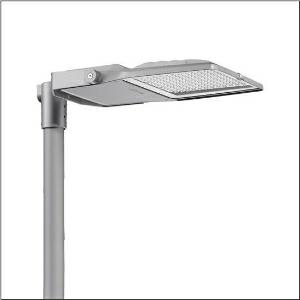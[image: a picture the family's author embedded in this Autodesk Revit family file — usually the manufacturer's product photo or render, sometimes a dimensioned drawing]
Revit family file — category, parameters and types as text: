
# Revit family: floodlight_fl_21_midi___pl33t_5xa7782f4f3a_2082
name_source: partatom
category: Lighting Fixtures
units: mm (PartAtom-declared; Revit-internal decimal feet)

## family parameters
Cut with Voids When Loaded = No
Host = Face
Light Source = No
Part Type = Normal
Room Calculation Point = No
Round Connector Dimension = Use Diameter
Shared = No

## types (1)
- --- (1 x LED, 36900 lm, 270.2 W, 4000K)
    Apparent Load = 270 VA
    CIE Flux Codes = 26 75 99 100 100
    Color Rendering = 70
    Color Temperature = 4000K
    Default Elevation = 1800 mm
    Description = Floodlight FL 21 midi, floodlight, primary light control with lens, of PMMA, primary optical cover: protective disc, of toughened safety glass, transparent, light distribution: PL33T, light emission: direct distribution, installation type: surface-mounted, LED, High Power LED, rated luminous flux: 36.900lm, luminous efficacy: 136lm/W, light colour: 740, colour temperature: 4000K, control gear: ECG iQ, control: optimised constant luminous flux control (CLO 2.0), Desk-Remote (wireless, voltage-free reading and setting of iQ features in the workshop via application-optimized NFC function/RFID function), Smart-Wire, Night-Set, Temp-Guard, Auto-Match, Street-Remote, with terminal, 6-pole, mains connection: 220..240V, AC, 50/60Hz, start of lifetime: 270W, end of lifetime: 286W, reduction: 136W, luminaire housing, of diecast aluminium, powder-coated, Siteco® metallic grey (DB 702S), corrosivity category C5 according to DIN EN ISO 12944, mast bracket, of steel, galvanised, powder-coated, Siteco® metallic grey (DB 702S), protection rating (complete): IP66, insulation class (complete): insulation class II (safety insulation), certification: CE, protection symbol: D, impact resistance: IK08, permissible operating ambient temperature: -40..+40°C, permissible operating ambient temperature for outdoor applications: -40..+50°C, standard: DIN EN 12944, packaging unit: 1 piece

Light Distribution: PL33T
    Height = 76 mm
    Lamp = 1 x LED
    Lamp Light Flux = 36900 lm
    Lamp Power = 270.2 W
    Lamp count = 1
    Length = 657 mm
    Luminous efficacy = 137 lm/W
    Manufacturer = Siteco
    ModVariant = No
    Model = 5XA7782F4F3A
    Number of Poles = 1
    OnlyDefault = Yes
    Power Factor = 1
    Product Name = Floodlight FL 21 midi | PL33T
    Product group = floodlight | pylon top
    ProductGroupID = 6101
    Protection Class = Protection class II
    Protection Degree = IP 66
    RLX_Detail_Level = 1
    RlxData = <blob elided: 153493 chars, md5=8b57c743>
    Socket = socket
    Standby Power = 0 W
    System Light Flux = 36900 lm
    System Power = 270 W
    Type Comments = factory setting: luminous flux: 100 % | dim-lin: 254 | 620 mA
    Type Image = l_1007123.jpg
    URL = http://relux.com
    VarID = @adj_011865
    Voltage = 0 V
    Weight = 0.00 kg
    Width = 442 mm

## geometry (parser evidence)
native form markers: Blend x4, Sweep x15
no freeform markers — native parametric forms only
